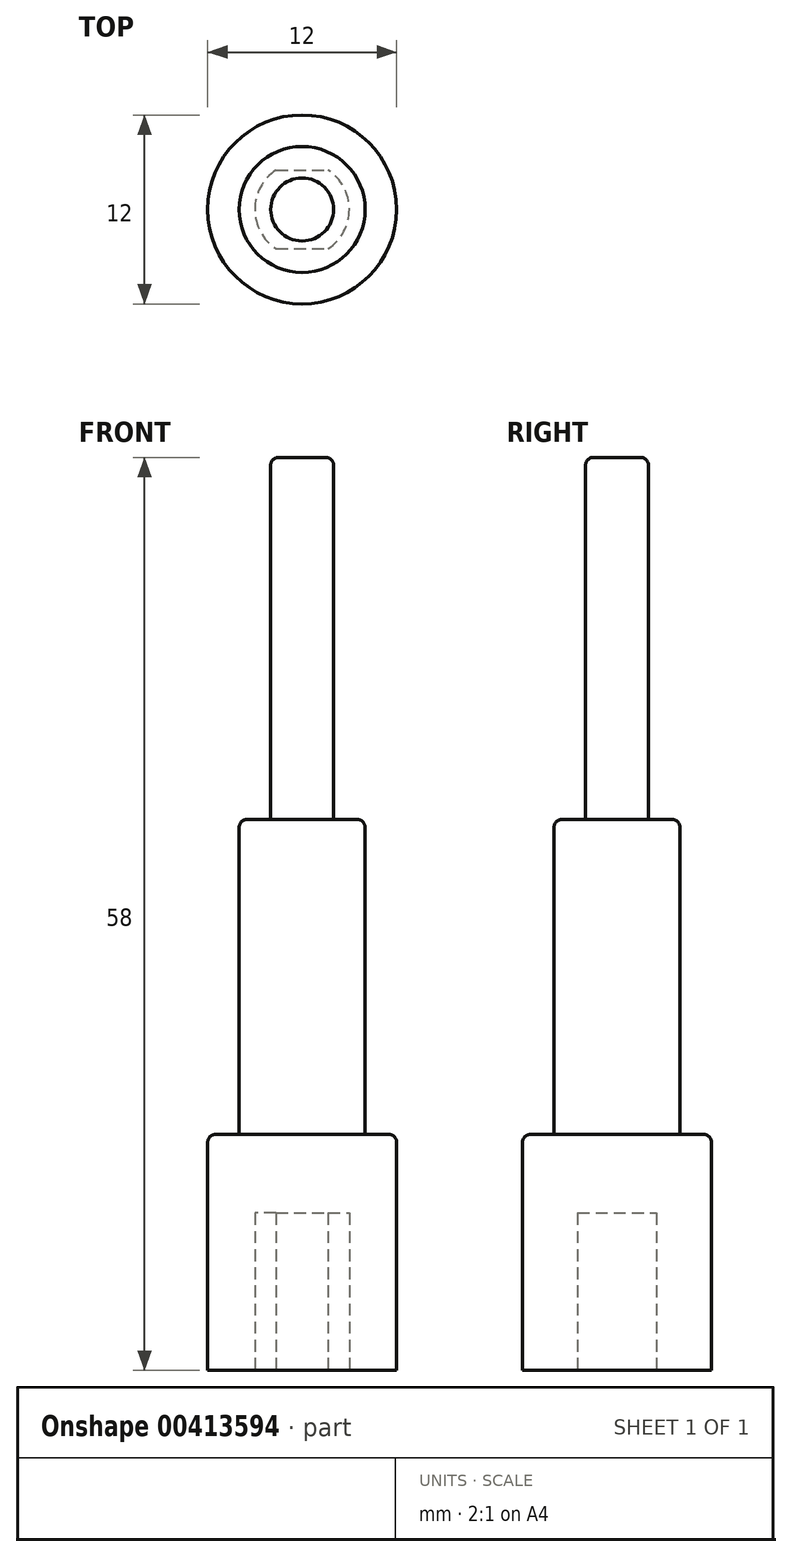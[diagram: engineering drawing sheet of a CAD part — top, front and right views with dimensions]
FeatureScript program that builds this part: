
annotation { "Feature Type Name" : "Feature", "Feature Type Description" : "" }
export const myFeature = defineFeature(function(context is Context, id is Id, definition is map)
    precondition{}
    {
        {
            var Q0;
            Q0=qCreatedBy(makeId("Top.planeOp"),FACE);
            var sketch = newSketch(context, id + "F0", { "sketchPlane" : qUnion([Q0])});
            skCircle(sketch, "E0", {"center": v(0, 0) * mm, "radius": 6 * mm});
            skSolve(sketch);
        }
        {
            var Q0;
            Q0=makeQuery(id+"F0.imprint","IMPRINT",FACE,{"disambiguationData":[TD([[makeQuery(id+"F0.imprint","IMPRINT",EDGE,{"derivedFrom":sQuery(id+"F0.wireOp",EDGE,"E0")}),1.0]])]});
            extrude(context, id + "F1", {"entities" : qUnion([Q0]), "depth" : 15 * mm});
        }
        {
            var Q0;
            Q0=makeQuery(id+"F1.opExtrude","CAP_FACE",FACE,{"disambiguationData":[OSD([sQuery(id+"F0.wireOp",EDGE,"E0")])],"isStart":false});
            var sketch = newSketch(context, id + "F2", { "sketchPlane" : qUnion([Q0])});
            skCircle(sketch, "E1", {"center": v(0, 0) * mm, "radius": 4 * mm});
            skSolve(sketch);
        }
        {
            var Q0;
            Q0=makeQuery(id+"F2.imprint","IMPRINT",FACE,{"disambiguationData":[TD([[makeQuery(id+"F2.imprint","IMPRINT",EDGE,{"derivedFrom":sQuery(id+"F2.wireOp",EDGE,"E1")}),1.0]])]});
            extrude(context, id + "F3", {"entities" : qUnion([Q0]), "operationType" : NewBodyOperationType.ADD, "depth" : 20 * mm});
        }
        {
            var Q0;
            Q0=makeQuery(id+"F3.opExtrude","CAP_FACE",FACE,{"disambiguationData":[OSD([sQuery(id+"F2.wireOp",EDGE,"E1")])],"isStart":false});
            var sketch = newSketch(context, id + "F4", { "sketchPlane" : qUnion([Q0])});
            skCircle(sketch, "E2", {"center": v(0, 0) * mm, "radius": 2 * mm});
            skSolve(sketch);
        }
        {
            var Q0;
            Q0=makeQuery(id+"F4.imprint","IMPRINT",FACE,{"disambiguationData":[TD([[makeQuery(id+"F4.imprint","IMPRINT",EDGE,{"derivedFrom":sQuery(id+"F4.wireOp",EDGE,"E2")}),1.0]])]});
            extrude(context, id + "F5", {"entities" : qUnion([Q0]), "operationType" : NewBodyOperationType.ADD, "depth" : 23 * mm});
        }
        {
            var Q0;
            Q0=makeQuery(id+"F3.opExtrude","CAP_EDGE",EDGE,{"disambiguationData":[OSD([sQuery(id+"F2.wireOp",EDGE,"E1")])],"isStart":false});
            var Q1;
            Q1=makeQuery(id+"F1.opExtrude","CAP_EDGE",EDGE,{"disambiguationData":[OSD([sQuery(id+"F0.wireOp",EDGE,"E0")])],"isStart":false});
            var Q2;
            Q2=makeQuery(id+"F5.opExtrude","CAP_EDGE",EDGE,{"disambiguationData":[OSD([sQuery(id+"F4.wireOp",EDGE,"E2")])],"isStart":false});
            fillet(context, id + "F6", {"entities" : qUnion([Q0, Q1, Q2]), "radius" : .5 * mm, "tangentPropagation" : true, "allowEdgeOverflow" : false});
        }
        {
            var Q0;
            Q0=makeQuery(id+"F1.opExtrude","CAP_FACE",FACE,{"disambiguationData":[OSD([sQuery(id+"F0.wireOp",EDGE,"E0")])],"isStart":true});
            var sketch = newSketch(context, id + "F7", { "sketchPlane" : qUnion([Q0])});
            skLineSegment(sketch, "E3.bottom", {"start": v(-1.66, -2.5) * mm, "end": v(1.66, -2.5) * mm});
            skLineSegment(sketch, "E3.top", {"start": v(-1.66, 2.5) * mm, "end": v(1.66, 2.5) * mm});
            skPoint(sketch, "E3.middle", {"position": v(0, 0) * mm});
            skArc(sketch, "E4", {"start": v(-1.66, 2.5) * mm, "mid": v(-3, 0) * mm, "end": v(-1.66, -2.5) * mm});
            skPoint(sketch, "E3.right.start.orphan", {"position": v(3.75, -2.5) * mm});
            skPoint(sketch, "E5.orphan", {"position": v(3.75, 2.5) * mm});
            skArc(sketch, "E6.trimOffspring", {"start": v(1.66, -2.5) * mm, "mid": v(3, 0) * mm, "end": v(1.66, 2.5) * mm});
            skPoint(sketch, "E3.left.end.orphan", {"position": v(-3.75, 2.5) * mm});
            skPoint(sketch, "E3.left.start.orphan", {"position": v(-3.75, -2.5) * mm});
            skSolve(sketch);
        }
        {
            var Q0;
            Q0=makeQuery(id+"F7.imprint","IMPRINT",FACE,{"disambiguationData":[TD([[makeQuery(id+"F7.imprint","IMPRINT",EDGE,{"derivedFrom":sQuery(id+"F7.wireOp",EDGE,"E3.bottom")}),1.0]])]});
            extrude(context, id + "F8", {"entities" : qUnion([Q0]), "operationType" : NewBodyOperationType.REMOVE, "oppositeDirection" : true, "depth" : 10 * mm});
        }
    });
